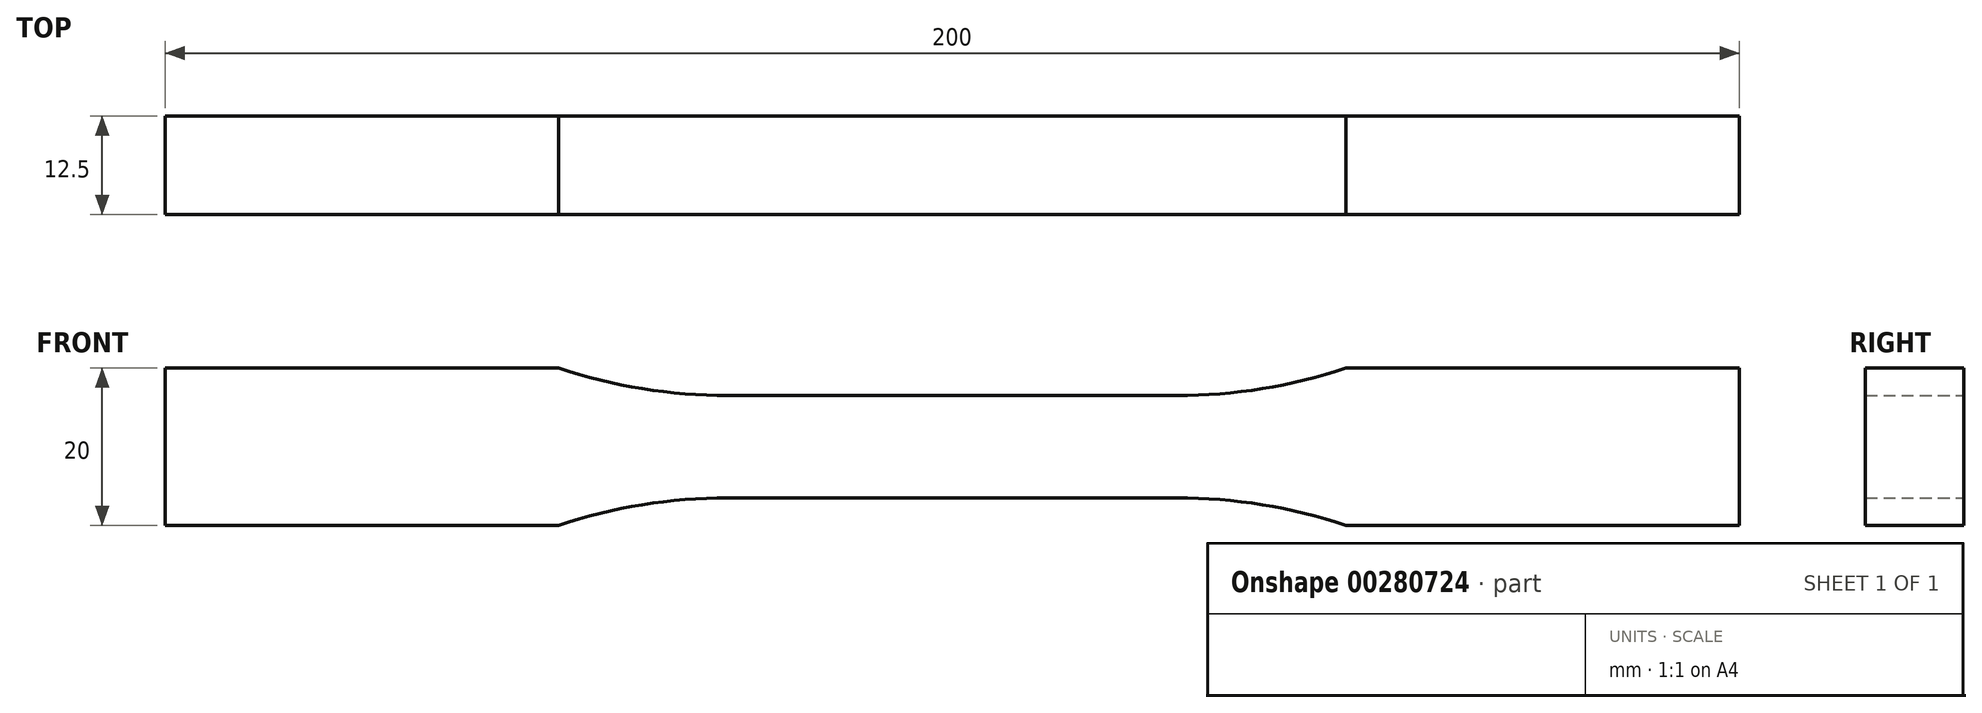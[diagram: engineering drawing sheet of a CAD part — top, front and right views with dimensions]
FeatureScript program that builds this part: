
annotation { "Feature Type Name" : "Feature", "Feature Type Description" : "" }
export const myFeature = defineFeature(function(context is Context, id is Id, definition is map)
    precondition{}
    {
        {
            var Q0;
            Q0=qCreatedBy(makeId("Front.planeOp"),FACE);
            var sketch = newSketch(context, id + "F0", { "sketchPlane" : qUnion([Q0])});
            skLineSegment(sketch, "E0", {"start": v(0, 6.49) * mm, "end": v(28.5, 6.49) * mm});
            skArc(sketch, "E1", {"start": v(28.5, 6.49) * mm, "mid": v(39.4, 7.37) * mm, "end": v(50, 10) * mm});
            skLineSegment(sketch, "E2", {"start": v(50, 10) * mm, "end": v(100, 10) * mm});
            skLineSegment(sketch, "E3", {"start": v(100, 10) * mm, "end": v(100, 0) * mm});
            skLineSegment(sketch, "E4.MirrorCS", {"start": v(-100, 10) * mm, "end": v(-100, 0) * mm});
            skLineSegment(sketch, "E5.MirrorCS", {"start": v(0, 6.49) * mm, "end": v(-28.5, 6.49) * mm});
            skLineSegment(sketch, "E6.MirrorCS", {"start": v(-50, 10) * mm, "end": v(-100, 10) * mm});
            skArc(sketch, "E7.MirrorCS", {"start": v(-28.5, 6.49) * mm, "mid": v(-39.4, 7.37) * mm, "end": v(-50, 10) * mm});
            skArc(sketch, "E8.MirrorCS", {"start": v(-28.5, -6.49) * mm, "mid": v(-39.4, -7.37) * mm, "end": v(-50, -10) * mm});
            skLineSegment(sketch, "E9.MirrorCS", {"start": v(-50, -10) * mm, "end": v(-100, -10) * mm});
            skLineSegment(sketch, "E10.MirrorCS", {"start": v(0, -6.49) * mm, "end": v(28.5, -6.49) * mm});
            skArc(sketch, "E11.MirrorCS", {"start": v(28.5, -6.49) * mm, "mid": v(39.4, -7.37) * mm, "end": v(50, -10) * mm});
            skLineSegment(sketch, "E12.MirrorCS", {"start": v(50, -10) * mm, "end": v(100, -10) * mm});
            skLineSegment(sketch, "E13.MirrorCS", {"start": v(100, -10) * mm, "end": v(100, 0) * mm});
            skLineSegment(sketch, "E14.MirrorCS", {"start": v(0, -6.49) * mm, "end": v(-28.5, -6.49) * mm});
            skLineSegment(sketch, "E15.MirrorCS", {"start": v(-100, -10) * mm, "end": v(-100, 0) * mm});
            skSolve(sketch);
        }
        {
            var Q0;
            Q0 = qSketchRegion(id + "F0", true);
            extrude(context, id + "F1", {"entities" : qUnion([Q0]), "endBound" : BoundingType.SYMMETRIC, "depth" : 12.5 * mm});
        }
    });
